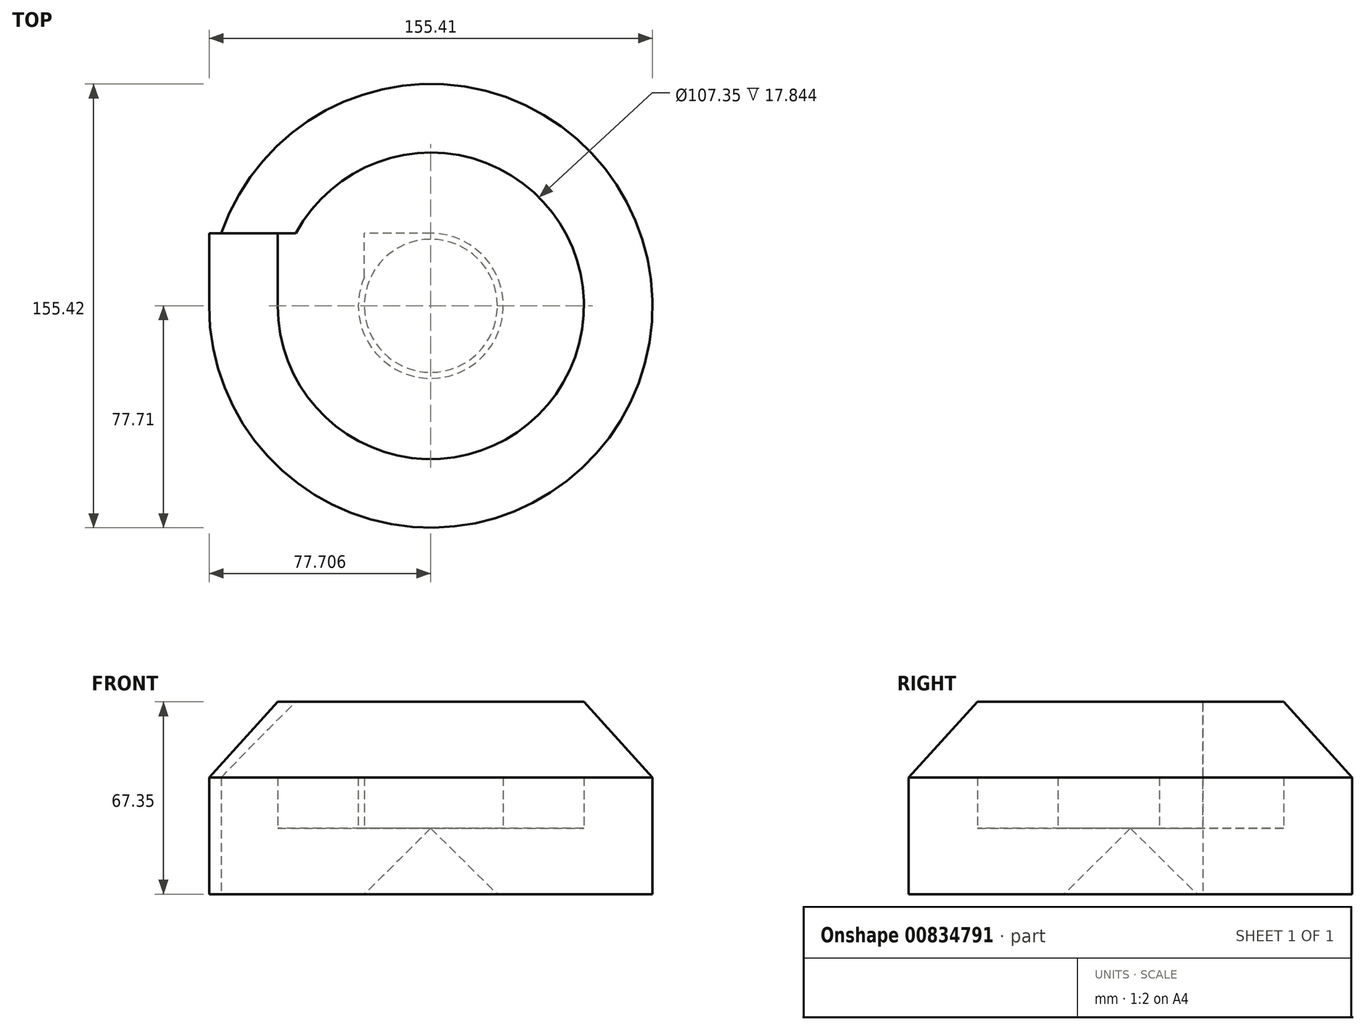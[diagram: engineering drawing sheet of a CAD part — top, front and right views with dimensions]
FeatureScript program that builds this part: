
annotation { "Feature Type Name" : "Feature", "Feature Type Description" : "" }
export const myFeature = defineFeature(function(context is Context, id is Id, definition is map)
    precondition{}
    {
        {
            var Q0;
            Q0=qCreatedBy(makeId("Front.planeOp"),FACE);
            var sketch = newSketch(context, id + "F0", { "sketchPlane" : qUnion([Q0])});
            skLineSegment(sketch, "E0.bottom", {"start": v(-24.03, 28.35) * mm, "end": v(30.36, 28.35) * mm});
            skLineSegment(sketch, "E0.top", {"start": v(-24.03, -12.52) * mm, "end": v(30.36, -12.52) * mm});
            skLineSegment(sketch, "E0.left", {"start": v(-24.03, 28.35) * mm, "end": v(-24.03, -12.52) * mm});
            skLineSegment(sketch, "E0.right", {"start": v(30.36, 28.35) * mm, "end": v(30.36, -12.52) * mm});
            skLineSegment(sketch, "E1.bottom", {"start": v(0, 10.5) * mm, "end": v(53.68, 10.5) * mm});
            skLineSegment(sketch, "E1.top", {"start": v(0, 54.83) * mm, "end": v(53.68, 54.83) * mm});
            skLineSegment(sketch, "E1.left", {"start": v(0, 10.5) * mm, "end": v(0, 54.83) * mm});
            skLineSegment(sketch, "E1.right", {"start": v(53.68, 10.5) * mm, "end": v(53.68, 54.83) * mm});
            skLineSegment(sketch, "E2", {"start": v(0, 54.83) * mm, "end": v(-24.03, 28.35) * mm});
            skLineSegment(sketch, "E3", {"start": v(53.68, 10.5) * mm, "end": v(30.36, -12.52) * mm});
            skLineSegment(sketch, "E4", {"start": v(53.68, 54.83) * mm, "end": v(30.36, 28.35) * mm});
            skLineSegment(sketch, "E5", {"start": v(0, 10.5) * mm, "end": v(-24.03, -12.52) * mm});
            skSolve(sketch);
        }
        {
            var Q0;
            Q0 = qSketchRegion(id + "F0", true);
            extrude(context, id + "F1", {"entities" : qUnion([Q0]), "depth" : 25.4 * mm, "offsetDistance" : 25.4 * mm});
        }
        {
            var Q0;
            Q0=makeQuery(id+"F1.opExtrude","SWEPT_FACE",FACE,{"disambiguationData":[OSD([sQuery(id+"F0.wireOp",EDGE,"E1.right")])]});
            var Q1;
            Q1=makeQuery(id+"F1.opExtrude","CAP_FACE",FACE,{"disambiguationData":[OSD([sQuery(id+"F0.wireOp",EDGE,"E0.bottom"),sQuery(id+"F0.wireOp",EDGE,"E0.top"),sQuery(id+"F0.wireOp",EDGE,"E0.left"),sQuery(id+"F0.wireOp",EDGE,"E0.right"),sQuery(id+"F0.wireOp",EDGE,"E1.bottom"),sQuery(id+"F0.wireOp",EDGE,"E1.top"),sQuery(id+"F0.wireOp",EDGE,"E1.left"),sQuery(id+"F0.wireOp",EDGE,"E1.right"),sQuery(id+"F0.wireOp",EDGE,"E2"),sQuery(id+"F0.wireOp",EDGE,"E3")])],"isStart":false});
            var Q2;
            Q2=makeQuery(id+"F1.opExtrude","CAP_EDGE",EDGE,{"disambiguationData":[OSD([sQuery(id+"F0.wireOp",EDGE,"E1.right")])],"isStart":false});
            revolve(context, id + "F2", {"operationType" : NewBodyOperationType.ADD, "surfaceOperationType" : NewSurfaceOperationType.NEW, "entities" : qUnion([Q0, Q1]), "axis" : qUnion([Q2]), "revolveType" : RevolveType.FULL});
        }
    });
